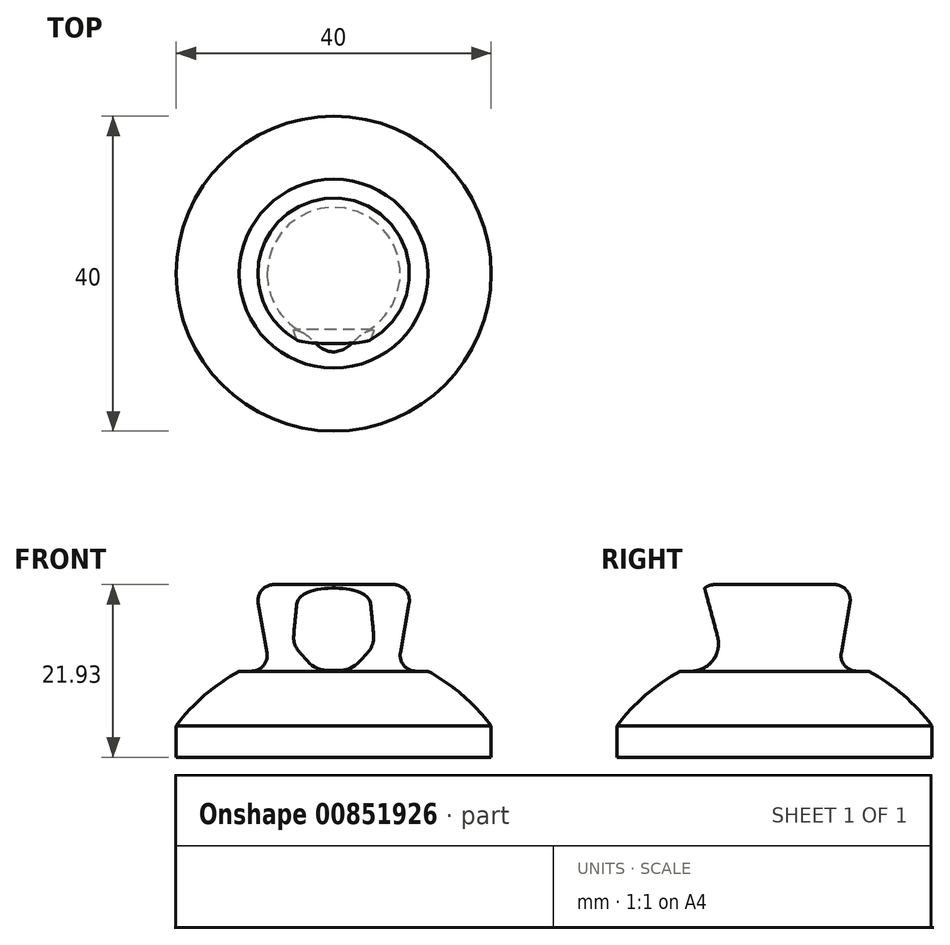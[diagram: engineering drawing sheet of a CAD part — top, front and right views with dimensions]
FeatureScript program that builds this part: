
annotation { "Feature Type Name" : "Feature", "Feature Type Description" : "" }
export const myFeature = defineFeature(function(context is Context, id is Id, definition is map)
    precondition{}
    {
        {
            var Q0;
            Q0=qCreatedBy(makeId("Top.planeOp"),FACE);
            var sketch = newSketch(context, id + "F0", { "sketchPlane" : qUnion([Q0])});
            skCircle(sketch, "E0", {"center": v(0, 0) * mm, "radius": 20 * mm});
            skSolve(sketch);
        }
        {
            var Q0;
            Q0=makeQuery(id+"F0.imprint","IMPRINT",FACE,{"disambiguationData":[TD([[makeQuery(id+"F0.imprint","IMPRINT",EDGE,{"derivedFrom":sQuery(id+"F0.wireOp",EDGE,"E0")}),1.0]])]});
            extrude(context, id + "F1", {"entities" : qUnion([Q0]), "depth" : 4 * mm, "offsetDistance" : 25 * mm});
        }
        {
            var Q0;
            Q0=qCreatedBy(makeId("Right.planeOp"),FACE);
            var sketch = newSketch(context, id + "F2", { "sketchPlane" : qUnion([Q0])});
            skLineSegment(sketch, "E1.0", {"start": v(-20, 4) * mm, "end": v(20, 4) * mm});
            skArc(sketch, "E2", {"start": v(20, 4) * mm, "mid": v(16.37, 7.9) * mm, "end": v(12, 10.93) * mm});
            skLineSegment(sketch, "E3", {"start": v(12, 10.93) * mm, "end": v(-12, 10.93) * mm});
            skArc(sketch, "E4.trimOffspring", {"start": v(-12, 10.93) * mm, "mid": v(-16.37, 7.9) * mm, "end": v(-20, 4) * mm});
            skLineSegment(sketch, "E5", {"start": v(0, 10.93) * mm, "end": v(0, 4) * mm});
            skLineSegment(sketch, "E6", {"start": v(8.06, 10.93) * mm, "end": v(10, 21.93) * mm});
            skLineSegment(sketch, "E7", {"start": v(10, 21.93) * mm, "end": v(0, 21.93) * mm});
            skLineSegment(sketch, "E8", {"start": v(0, 21.93) * mm, "end": v(0, 10.93) * mm});
            skSolve(sketch);
        }
        {
            var Q0;
            {var subQ0=sQuery(id+"F2.wireOp",EDGE,"E2");Q0=makeQuery(id+"F2.imprint","IMPRINT",FACE,{"disambiguationData":[TD([[makeQuery(id+"F2.imprint","IMPRINT",EDGE,{"derivedFrom":subQ0}),1.0]])]});}
            var Q1;
            {var subQ2=sQuery(id+"F2.wireOp",EDGE,"E6");Q1=makeQuery(id+"F2.imprint","IMPRINT",FACE,{"disambiguationData":[TD([[makeQuery(id+"F2.imprint","IMPRINT",EDGE,{"derivedFrom":subQ2}),1.0]])]});}
            var Q2;
            Q2=sQuery(id+"F2.wireOp",EDGE,"E5");
            revolve(context, id + "F3", {"operationType" : NewBodyOperationType.ADD, "surfaceOperationType" : NewSurfaceOperationType.NEW, "entities" : qUnion([Q0, Q1]), "axis" : qUnion([Q2]), "revolveType" : RevolveType.FULL});
        }
        {
            var Q0;
            Q0=makeQuery(id+"F3.opRevolve","SWEPT_EDGE",EDGE,{"disambiguationData":[OSD([sQuery(id+"F2.wireOp",EDGE,"E3"),sQuery(id+"F2.wireOp",EDGE,"E6")])]});
            fillet(context, id + "F4", {"entities" : qUnion([Q0]), "radius" : 2 * mm, "tangentPropagation" : true, "allowEdgeOverflow" : false});
        }
        {
            var Q0;
            Q0=makeQuery(id+"F3.opRevolve","SWEPT_EDGE",EDGE,{"disambiguationData":[OSD([sQuery(id+"F2.wireOp",EDGE,"E6"),sQuery(id+"F2.wireOp",EDGE,"E7")])]});
            fillet(context, id + "F5", {"entities" : qUnion([Q0]), "radius" : 2 * mm, "tangentPropagation" : true, "allowEdgeOverflow" : false});
        }
        {
            var Q0;
            Q0=qCreatedBy(makeId("Right.planeOp"),FACE);
            var sketch = newSketch(context, id + "F6", { "sketchPlane" : qUnion([Q0])});
            skLineSegment(sketch, "E9.0", {"start": v(-12, 10.93) * mm, "end": v(-10.61, 10.93) * mm});
            skLineSegment(sketch, "E10", {"start": v(-7.23, 15.34) * mm, "end": v(-9, 21.93) * mm});
            skLineSegment(sketch, "E11", {"start": v(-9, 21.93) * mm, "end": v(-12, 21.93) * mm});
            skLineSegment(sketch, "E12", {"start": v(-12, 21.93) * mm, "end": v(-12, 10.93) * mm});
            skLineSegment(sketch, "E13", {"start": v(7.62, 21.93) * mm, "end": v(-7.62, 21.93) * mm});
            skPoint(sketch, "E14.newPointB", {"position": v(12, 10.93) * mm});
            skArc(sketch, "E14.filletArc", {"start": v(-10.61, 10.93) * mm, "mid": v(-7.84, 12.3) * mm, "end": v(-7.23, 15.34) * mm});
            skSolve(sketch);
        }
        {
            var Q0;
            {var subQ2=sQuery(id+"F6.wireOp",EDGE,"E10");Q0=makeQuery(id+"F6.imprint","IMPRINT",FACE,{"disambiguationData":[TD([[makeQuery(id+"F6.imprint","IMPRINT",EDGE,{"derivedFrom":subQ2}),1.0]])]});}
            extrude(context, id + "F7", {"entities" : qUnion([Q0]), "operationType" : NewBodyOperationType.REMOVE, "endBound" : BoundingType.THROUGH_ALL, "depth" : 25 * mm, "offsetDistance" : 25 * mm, "hasSecondDirection" : true, "secondDirectionBound" : BoundingType.THROUGH_ALL, "secondDirectionOppositeDirection" : true, "secondDirectionDepth" : 25 * mm});
        }
    });
